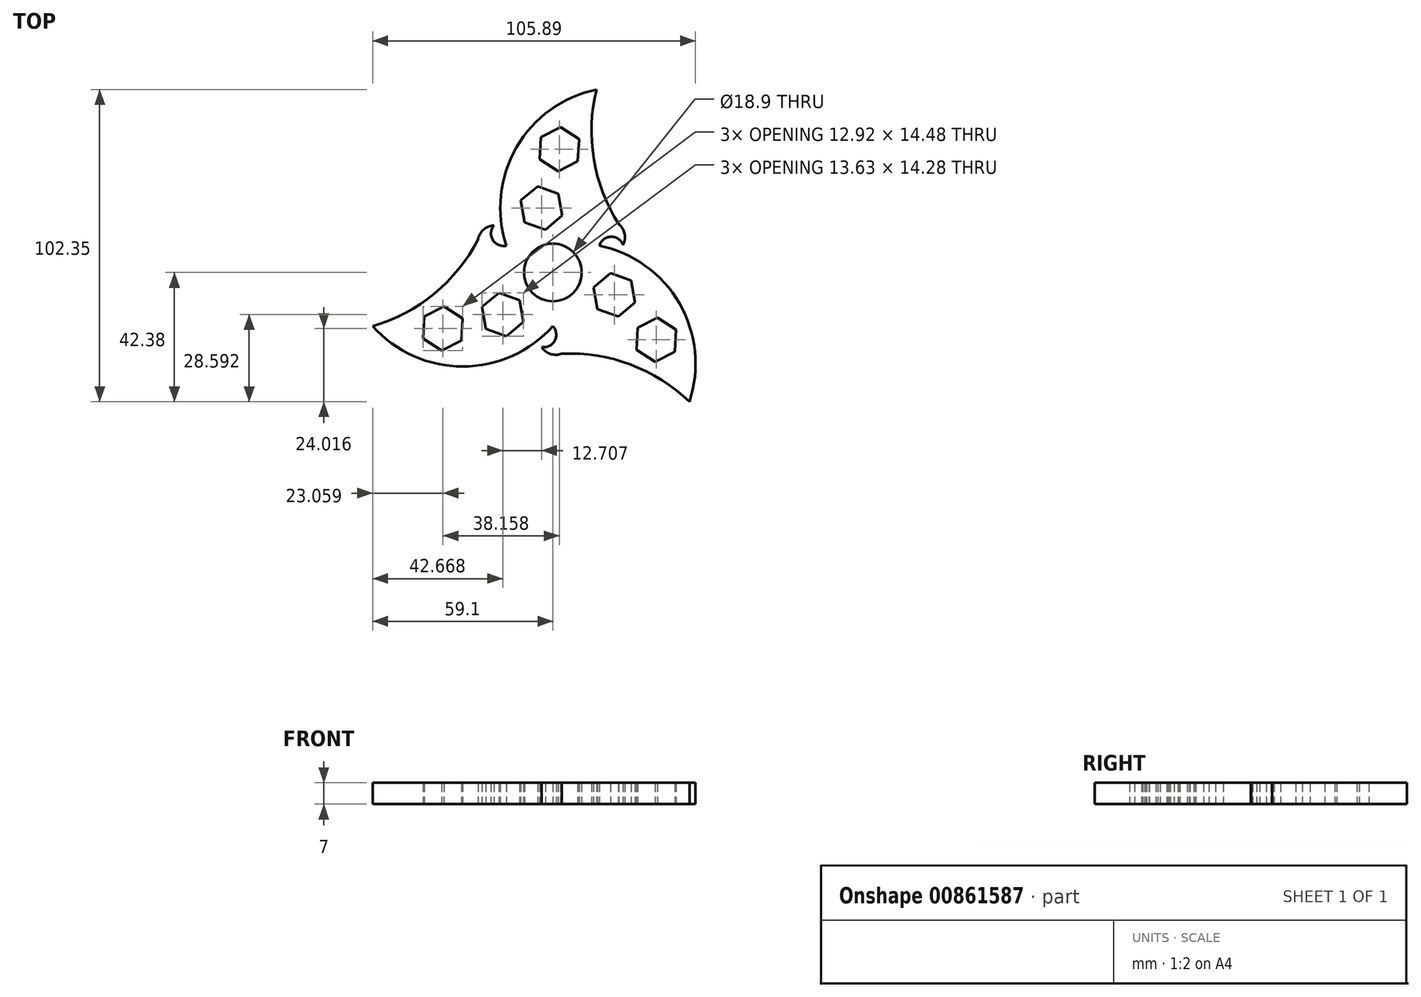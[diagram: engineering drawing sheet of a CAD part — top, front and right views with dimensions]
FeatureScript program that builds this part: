
annotation { "Feature Type Name" : "Feature", "Feature Type Description" : "" }
export const myFeature = defineFeature(function(context is Context, id is Id, definition is map)
    precondition{}
    {
        {
            var Q0;
            Q0=qCreatedBy(makeId("Top.planeOp"),FACE);
            var sketch = newSketch(context, id + "F0", { "sketchPlane" : qUnion([Q0])});
            skCircle(sketch, "E0", {"center": v(0, 0) * mm, "radius": 9.45 * mm});
            skArc(sketch, "E1", {"start": v(-59.1, -17.59) * mm, "mid": v(-38.9, -6.96) * mm, "end": v(-24.56, 10.8) * mm});
            skArc(sketch, "E2", {"start": v(-59.1, -17.59) * mm, "mid": v(-29.55, -30.86) * mm, "end": v(0, -17.59) * mm});
            skArc(sketch, "E3.1.0", {"start": v(44.78, -42.38) * mm, "mid": v(25.47, -30.2) * mm, "end": v(2.92, -26.67) * mm});
            skArc(sketch, "E3.1.1", {"start": v(44.78, -42.38) * mm, "mid": v(41.5, -10.16) * mm, "end": v(15.23, 8.8) * mm});
            skArc(sketch, "E3.2.0", {"start": v(14.32, 59.97) * mm, "mid": v(13.42, 37.16) * mm, "end": v(21.64, 15.86) * mm});
            skArc(sketch, "E3.2.1", {"start": v(14.32, 59.97) * mm, "mid": v(-11.95, 41.02) * mm, "end": v(-15.23, 8.8) * mm});
            skArc(sketch, "E4", {"start": v(-19.33, 15.45) * mm, "mid": v(-22.74, 14.03) * mm, "end": v(-24.56, 10.8) * mm});
            skArc(sketch, "E5", {"start": v(-19.33, 15.45) * mm, "mid": v(-19.68, 10.65) * mm, "end": v(-15.23, 8.8) * mm});
            skArc(sketch, "E6.1.0", {"start": v(-3.72, -24.47) * mm, "mid": v(-0.78, -26.71) * mm, "end": v(2.92, -26.67) * mm});
            skArc(sketch, "E6.1.1", {"start": v(-3.72, -24.47) * mm, "mid": v(0.62, -22.37) * mm, "end": v(0, -17.59) * mm});
            skArc(sketch, "E6.2.0", {"start": v(23.05, 9.01) * mm, "mid": v(23.52, 12.68) * mm, "end": v(21.64, 15.86) * mm});
            skArc(sketch, "E6.2.1", {"start": v(23.05, 9.01) * mm, "mid": v(19.06, 11.72) * mm, "end": v(15.23, 8.8) * mm});
            skLineSegment(sketch, "E7", {"start": v(0, 0) * mm, "end": v(3.22, 61.37) * mm, "construction": true});
            skCircle(sketch, "E8.cCircle", {"center": v(2.12, 40.4) * mm, "radius": 7.25 * mm, "construction": true});
            skLineSegment(sketch, "E8.0", {"start": v(2.5, 47.63) * mm, "end": v(8.58, 43.69) * mm});
            skLineSegment(sketch, "E8.1", {"start": v(8.58, 43.69) * mm, "end": v(8.2, 36.45) * mm});
            skLineSegment(sketch, "E8.2", {"start": v(8.2, 36.45) * mm, "end": v(1.74, 33.15) * mm});
            skLineSegment(sketch, "E8.3", {"start": v(1.74, 33.15) * mm, "end": v(-4.34, 37.1) * mm});
            skLineSegment(sketch, "E8.4", {"start": v(-4.34, 37.1) * mm, "end": v(-3.96, 44.34) * mm});
            skLineSegment(sketch, "E8.5", {"start": v(-3.96, 44.34) * mm, "end": v(2.5, 47.63) * mm});
            skLineSegment(sketch, "E9", {"start": v(0, 0) * mm, "end": v(-11.53, 65.37) * mm, "construction": true});
            skCircle(sketch, "E10.cCircle", {"center": v(-3.72, 21.12) * mm, "radius": 7.25 * mm, "construction": true});
            skLineSegment(sketch, "E10.0", {"start": v(-4.98, 28.26) * mm, "end": v(1.83, 25.78) * mm});
            skLineSegment(sketch, "E10.1", {"start": v(1.83, 25.78) * mm, "end": v(3.09, 18.64) * mm});
            skLineSegment(sketch, "E10.2", {"start": v(3.09, 18.64) * mm, "end": v(-2.47, 13.98) * mm});
            skLineSegment(sketch, "E10.3", {"start": v(-2.47, 13.98) * mm, "end": v(-9.28, 16.46) * mm});
            skLineSegment(sketch, "E10.4", {"start": v(-9.28, 16.46) * mm, "end": v(-10.54, 23.6) * mm});
            skLineSegment(sketch, "E10.5", {"start": v(-10.54, 23.6) * mm, "end": v(-4.98, 28.26) * mm});
            skLineSegment(sketch, "E11.1.0", {"start": v(-10.88, -9.13) * mm, "end": v(-9.62, -16.27) * mm});
            skLineSegment(sketch, "E11.1.1", {"start": v(-17.7, -6.65) * mm, "end": v(-10.88, -9.13) * mm});
            skLineSegment(sketch, "E11.1.2", {"start": v(-23.24, -11.3) * mm, "end": v(-17.7, -6.65) * mm});
            skLineSegment(sketch, "E11.1.3", {"start": v(-21.99, -18.45) * mm, "end": v(-23.24, -11.3) * mm});
            skLineSegment(sketch, "E11.1.4", {"start": v(-15.17, -20.93) * mm, "end": v(-21.99, -18.45) * mm});
            skLineSegment(sketch, "E11.1.5", {"start": v(-9.62, -16.27) * mm, "end": v(-15.17, -20.93) * mm});
            skLineSegment(sketch, "E11.1.6", {"start": v(-35.66, -11.12) * mm, "end": v(-29.58, -15.07) * mm});
            skLineSegment(sketch, "E11.1.7", {"start": v(-42.12, -14.42) * mm, "end": v(-35.66, -11.12) * mm});
            skLineSegment(sketch, "E11.1.8", {"start": v(-42.5, -21.66) * mm, "end": v(-42.12, -14.42) * mm});
            skLineSegment(sketch, "E11.1.9", {"start": v(-36.42, -25.6) * mm, "end": v(-42.5, -21.66) * mm});
            skLineSegment(sketch, "E11.1.10", {"start": v(-29.96, -22.31) * mm, "end": v(-36.42, -25.6) * mm});
            skLineSegment(sketch, "E11.1.11", {"start": v(-29.58, -15.07) * mm, "end": v(-29.96, -22.31) * mm});
            skLineSegment(sketch, "E11.2.0", {"start": v(13.34, -4.86) * mm, "end": v(18.9, -0.2) * mm});
            skLineSegment(sketch, "E11.2.1", {"start": v(14.6, -12) * mm, "end": v(13.34, -4.86) * mm});
            skLineSegment(sketch, "E11.2.2", {"start": v(21.42, -14.48) * mm, "end": v(14.6, -12) * mm});
            skLineSegment(sketch, "E11.2.3", {"start": v(26.97, -9.82) * mm, "end": v(21.42, -14.48) * mm});
            skLineSegment(sketch, "E11.2.4", {"start": v(25.71, -2.68) * mm, "end": v(26.97, -9.82) * mm});
            skLineSegment(sketch, "E11.2.5", {"start": v(18.9, -0.2) * mm, "end": v(25.71, -2.68) * mm});
            skLineSegment(sketch, "E11.2.6", {"start": v(27.46, -25.32) * mm, "end": v(27.84, -18.08) * mm});
            skLineSegment(sketch, "E11.2.7", {"start": v(33.54, -29.27) * mm, "end": v(27.46, -25.32) * mm});
            skLineSegment(sketch, "E11.2.8", {"start": v(40, -25.98) * mm, "end": v(33.54, -29.27) * mm});
            skLineSegment(sketch, "E11.2.9", {"start": v(40.38, -18.74) * mm, "end": v(40, -25.98) * mm});
            skLineSegment(sketch, "E11.2.10", {"start": v(34.3, -14.8) * mm, "end": v(40.38, -18.74) * mm});
            skLineSegment(sketch, "E11.2.11", {"start": v(27.84, -18.08) * mm, "end": v(34.3, -14.8) * mm});
            skSolve(sketch);
        }
        {
            var Q0;
            Q0=makeQuery(id+"F0.imprint","IMPRINT",FACE,{"disambiguationData":[TD([[makeQuery(id+"F0.imprint","IMPRINT",EDGE,{"derivedFrom":sQuery(id+"F0.wireOp",EDGE,"E0")}),-1.0]])]});
            extrude(context, id + "F1", {"entities" : qUnion([Q0]), "depth" : 7 * mm, "offsetDistance" : 25 * mm});
        }
    });
